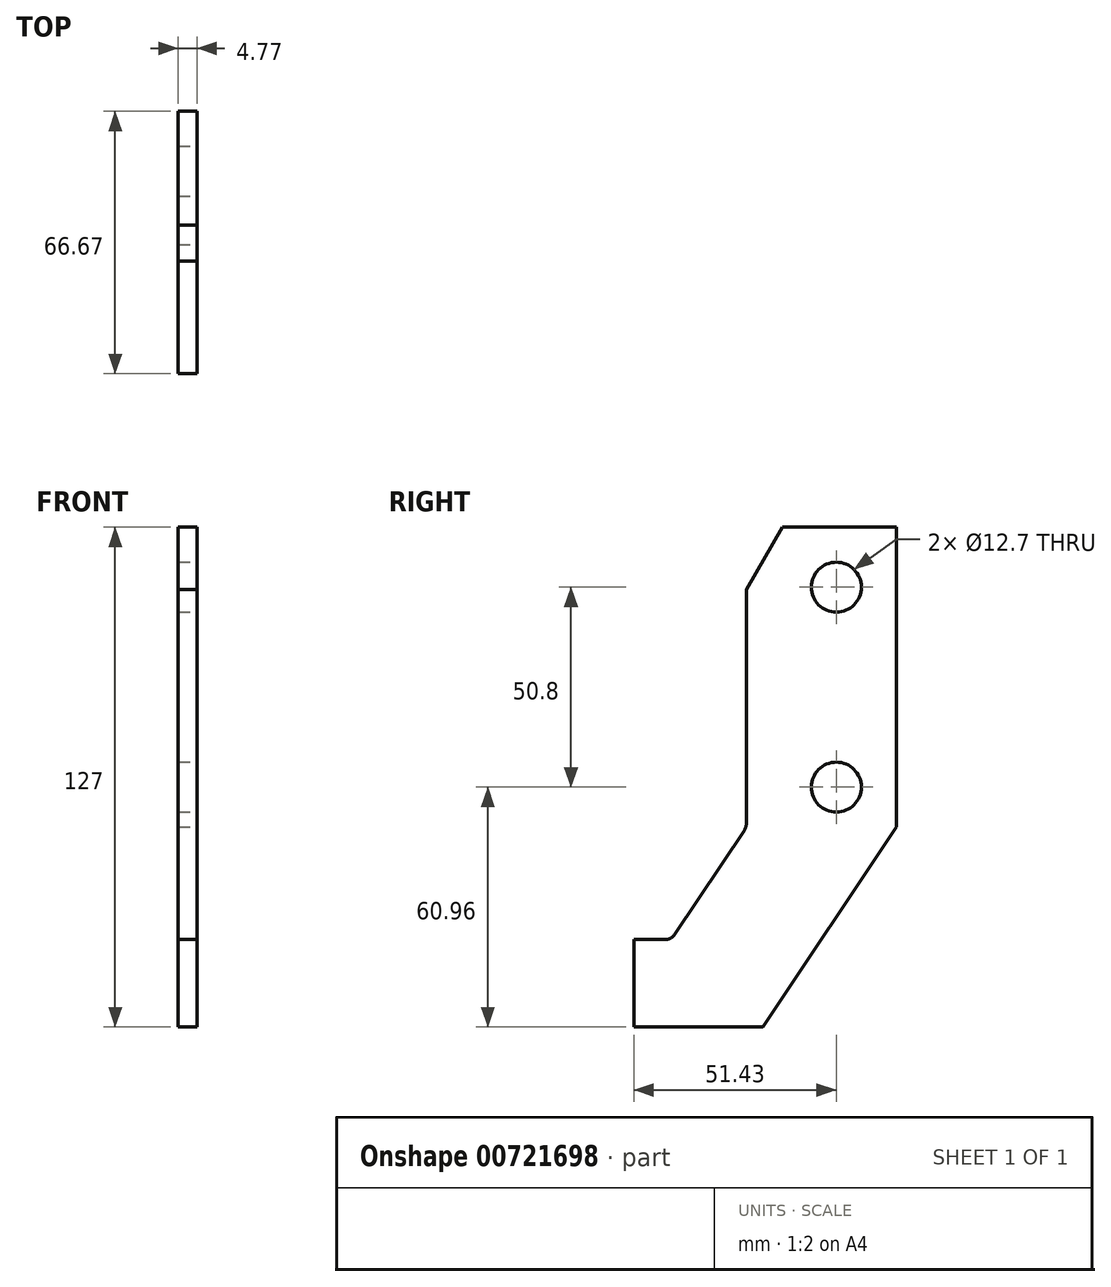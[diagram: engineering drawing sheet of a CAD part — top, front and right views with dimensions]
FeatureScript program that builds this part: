
annotation { "Feature Type Name" : "Feature", "Feature Type Description" : "" }
export const myFeature = defineFeature(function(context is Context, id is Id, definition is map)
    precondition{}
    {
        {
            var Q0;
            Q0=qCreatedBy(makeId("Top.planeOp"),FACE);
            var sketch = newSketch(context, id + "F0", { "sketchPlane" : qUnion([Q0])});
            skLineSegment(sketch, "E0", {"start": v(0, 62.17) * mm, "end": v(0, -63.7) * mm, "construction": true});
            skLineSegment(sketch, "E1", {"start": v(28.58, 0) * mm, "end": v(28.58, -127) * mm});
            skLineSegment(sketch, "E2.1", {"start": v(33.34, 0) * mm, "end": v(33.34, -127) * mm});
            skLineSegment(sketch, "E3", {"start": v(28.57, 0) * mm, "end": v(33.34, 0) * mm});
            skLineSegment(sketch, "E4", {"start": v(28.58, -127) * mm, "end": v(33.34, -127) * mm});
            skSolve(sketch);
        }
        {
            var Q0;
            Q0=qSketchRegion(id+"F0",true);
            extrude(context, id + "F1", {"entities" : qUnion([Q0]), "depth" : 127 * mm, "offsetDistance" : 25.4 * mm});
        }
        {
            var Q0;
            Q0=qCreatedBy(makeId("Right.planeOp"),FACE);
            var sketch = newSketch(context, id + "F2", { "sketchPlane" : qUnion([Q0])});
            skLineSegment(sketch, "E5", {"start": v(-15.24, 185.34) * mm, "end": v(-15.24, -10.43) * mm, "construction": true});
            skCircle(sketch, "E6", {"center": v(-15.24, 111.76) * mm, "radius": 6.35 * mm});
            skCircle(sketch, "E7", {"center": v(-15.24, 60.96) * mm, "radius": 6.35 * mm});
            skLineSegment(sketch, "E8", {"start": v(0, 50.8) * mm, "end": v(-33.87, 0) * mm});
            skLineSegment(sketch, "E9", {"start": v(0, 50.8) * mm, "end": v(0, 0) * mm});
            skLineSegment(sketch, "E10", {"start": v(0, 0) * mm, "end": v(-33.87, 0) * mm});
            skLineSegment(sketch, "E11", {"start": v(0, 50.8) * mm, "end": v(-65.09, 50.8) * mm, "construction": true});
            skLineSegment(sketch, "E12", {"start": v(-66.68, 0) * mm, "end": v(-127, 0) * mm});
            skLineSegment(sketch, "E13", {"start": v(-127, 0) * mm, "end": v(-127, 127) * mm});
            skLineSegment(sketch, "E14", {"start": v(-38.1, 111.12) * mm, "end": v(-28.93, 127) * mm});
            skLineSegment(sketch, "E15", {"start": v(-28.93, 127) * mm, "end": v(-127, 127) * mm});
            skLineSegment(sketch, "E16", {"start": v(-66.68, 22.23) * mm, "end": v(-57.15, 22.23) * mm});
            skLineSegment(sketch, "E17", {"start": v(-57.15, 22.23) * mm, "end": v(-38.1, 50.8) * mm});
            skLineSegment(sketch, "E18", {"start": v(-38.1, 50.8) * mm, "end": v(-38.1, 111.12) * mm});
            skLineSegment(sketch, "E19", {"start": v(-66.68, 22.23) * mm, "end": v(-66.68, 0) * mm});
            skSolve(sketch);
        }
        {
            var Q0;
            Q0=qSketchRegion(id+"F2",true);
            extrude(context, id + "F3", {"entities" : qUnion([Q0]), "operationType" : NewBodyOperationType.REMOVE, "endBound" : BoundingType.SYMMETRIC, "oppositeDirection" : true, "depth" : 101.6 * mm, "offsetDistance" : 25.4 * mm});
        }
        {
            var Q0;
            {var subQ0=sQuery(id+"F2.wireOp",EDGE,"E16");var subQ1=sQuery(id+"F2.wireOp",EDGE,"E17");Q0=makeQuery(id+"F3.boolean.opBoolean","COPY",EDGE,{"disambiguationData":[TD([makeQuery(id+"F1.opExtrude","SWEPT_FACE",FACE,{"disambiguationData":[OSD([sQuery(id+"F0.wireOp",EDGE,"E1")])]})])],"derivedFrom":makeQuery(id+"F3.opExtrude","SWEPT_EDGE",EDGE,{"disambiguationData":[OSD([subQ0,subQ1])]})});}
            var Q1;
            {var subQ0=sQuery(id+"F2.wireOp",EDGE,"E16");var subQ1=sQuery(id+"F2.wireOp",EDGE,"E17");Q1=makeQuery(id+"F3.boolean.opBoolean","COPY",EDGE,{"disambiguationData":[TD([makeQuery(id+"F1.opExtrude","SWEPT_FACE",FACE,{"disambiguationData":[OSD([sQuery(id+"F0.wireOp",EDGE,"b9828456-dbd4-4b47-8b77-68f3f45004e82.MirrorCS")])]})])],"derivedFrom":makeQuery(id+"F3.opExtrude","SWEPT_EDGE",EDGE,{"disambiguationData":[OSD([subQ0,subQ1])]})});}
            var Q2;
            {var subQ0=sQuery(id+"F2.wireOp",EDGE,"E17");var subQ1=sQuery(id+"F2.wireOp",EDGE,"E18");Q2=makeQuery(id+"F3.boolean.opBoolean","COPY",EDGE,{"disambiguationData":[TD([makeQuery(id+"F1.opExtrude","SWEPT_FACE",FACE,{"disambiguationData":[OSD([sQuery(id+"F0.wireOp",EDGE,"E1")])]})])],"derivedFrom":makeQuery(id+"F3.opExtrude","SWEPT_EDGE",EDGE,{"disambiguationData":[OSD([subQ0,subQ1])]})});}
            var Q3;
            {var subQ0=sQuery(id+"F2.wireOp",EDGE,"E17");var subQ1=sQuery(id+"F2.wireOp",EDGE,"E18");Q3=makeQuery(id+"F3.boolean.opBoolean","COPY",EDGE,{"disambiguationData":[TD([makeQuery(id+"F1.opExtrude","SWEPT_FACE",FACE,{"disambiguationData":[OSD([sQuery(id+"F0.wireOp",EDGE,"b9828456-dbd4-4b47-8b77-68f3f45004e82.MirrorCS")])]})])],"derivedFrom":makeQuery(id+"F3.opExtrude","SWEPT_EDGE",EDGE,{"disambiguationData":[OSD([subQ0,subQ1])]})});}
            fillet(context, id + "F4", {"entities" : qUnion([Q0, Q1, Q2, Q3]), "radius" : 3.17 * mm, "tangentPropagation" : true, "allowEdgeOverflow" : false});
        }
    });
